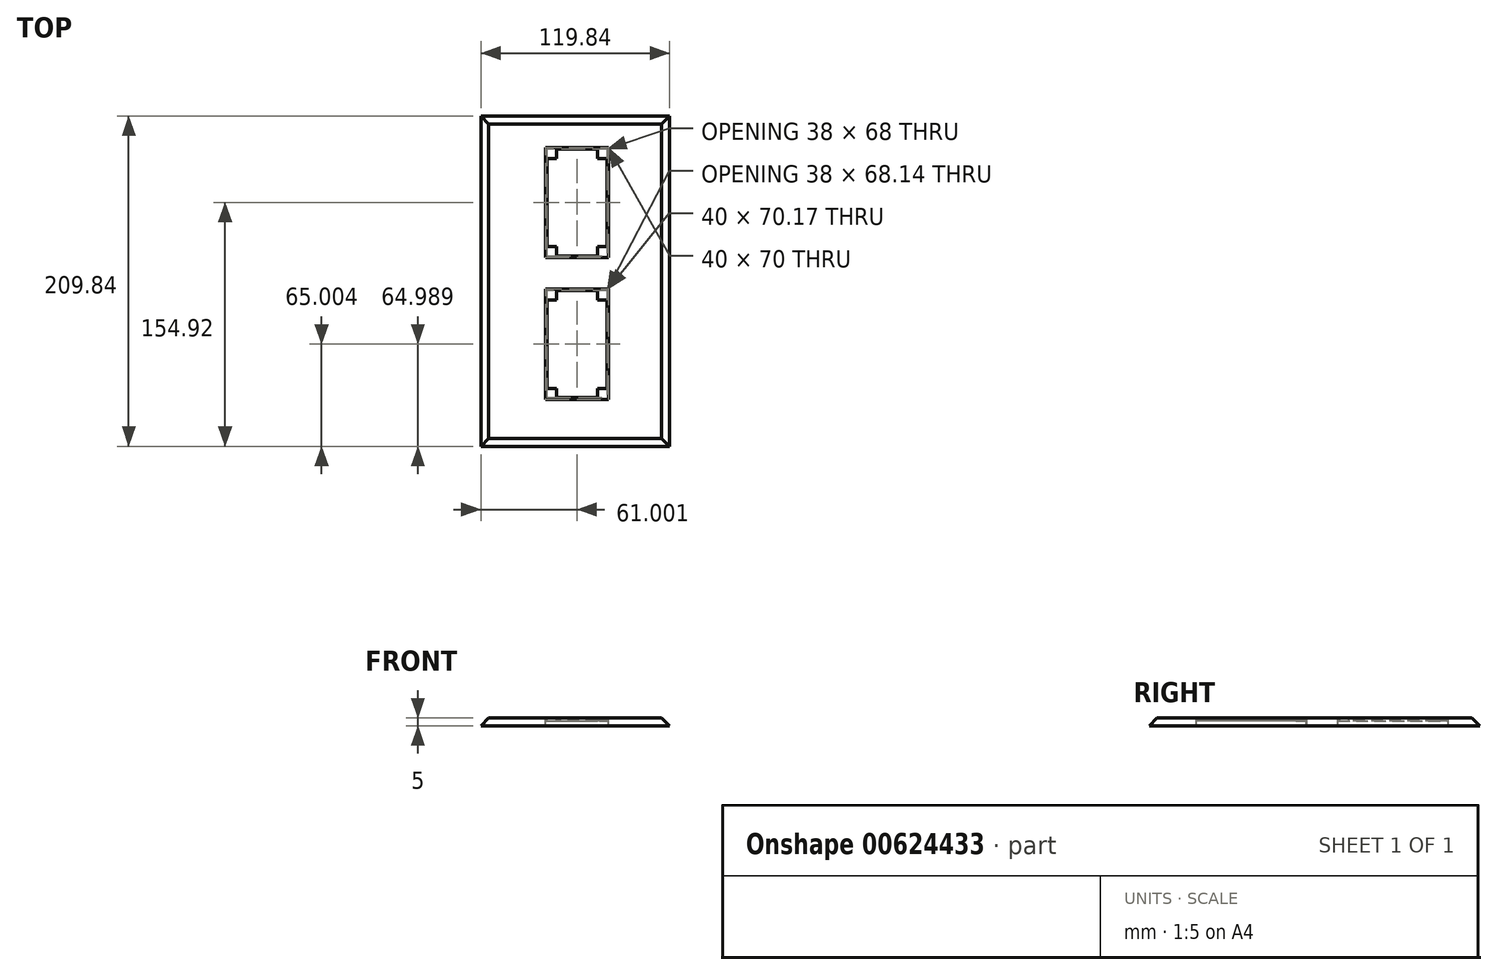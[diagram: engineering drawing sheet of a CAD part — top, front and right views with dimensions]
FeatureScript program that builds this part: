
annotation { "Feature Type Name" : "Feature", "Feature Type Description" : "" }
export const myFeature = defineFeature(function(context is Context, id is Id, definition is map)
    precondition{}
    {
        {
            var Q0;
            Q0=qCreatedBy(makeId("Top.planeOp"),FACE);
            var sketch = newSketch(context, id + "F0", { "sketchPlane" : qUnion([Q0])});
            skLineSegment(sketch, "E0.bottom", {"start": v(60, -105) * mm, "end": v(-60, -105) * mm});
            skLineSegment(sketch, "E0.top", {"start": v(60, 105) * mm, "end": v(-60, 105) * mm});
            skLineSegment(sketch, "E0.left", {"start": v(60, -105) * mm, "end": v(60, 105) * mm});
            skLineSegment(sketch, "E0.right", {"start": v(-60, -105) * mm, "end": v(-60, 105) * mm});
            skPoint(sketch, "E0.middle", {"position": v(0, 0) * mm});
            skLineSegment(sketch, "E1", {"start": v(-18.92, 52.2) * mm, "end": v(-18.92, 85) * mm});
            skLineSegment(sketch, "E2", {"start": v(21.08, 50.97) * mm, "end": v(21.08, 85) * mm});
            skLineSegment(sketch, "E3", {"start": v(21.08, 85) * mm, "end": v(-18.92, 85) * mm});
            skLineSegment(sketch, "E4", {"start": v(-18.92, 85) * mm, "end": v(-18.92, 15) * mm});
            skLineSegment(sketch, "E5", {"start": v(-18.92, 15) * mm, "end": v(21.08, 15) * mm});
            skLineSegment(sketch, "E6", {"start": v(21.08, 15) * mm, "end": v(21.08, 85) * mm});
            skPoint(sketch, "E7.start.orphan", {"position": v(26.42, 105) * mm});
            skPoint(sketch, "E8.orphan", {"position": v(21.08, 105) * mm});
            skLineSegment(sketch, "E9.bottom", {"start": v(-18.92, 85) * mm, "end": v(-11.92, 85) * mm});
            skLineSegment(sketch, "E9.top", {"start": v(-17.92, 78) * mm, "end": v(-11.92, 78) * mm});
            skLineSegment(sketch, "E9.left", {"start": v(-18.92, 85) * mm, "end": v(-18.92, 78) * mm});
            skLineSegment(sketch, "E9.right", {"start": v(-11.92, 84) * mm, "end": v(-11.92, 78) * mm});
            skLineSegment(sketch, "E10.bottom", {"start": v(-18.92, 15) * mm, "end": v(-11.92, 15) * mm});
            skLineSegment(sketch, "E10.top", {"start": v(-17.92, 22) * mm, "end": v(-11.92, 22) * mm});
            skLineSegment(sketch, "E10.left", {"start": v(-18.92, 15) * mm, "end": v(-18.92, 22) * mm});
            skLineSegment(sketch, "E10.right", {"start": v(-11.92, 16) * mm, "end": v(-11.92, 22) * mm});
            skLineSegment(sketch, "E11.bottom", {"start": v(21.08, 85) * mm, "end": v(14.08, 85) * mm});
            skLineSegment(sketch, "E11.top", {"start": v(20.08, 78) * mm, "end": v(14.08, 78) * mm});
            skLineSegment(sketch, "E11.left", {"start": v(21.08, 85) * mm, "end": v(21.08, 78) * mm});
            skLineSegment(sketch, "E11.right", {"start": v(14.08, 84) * mm, "end": v(14.08, 78) * mm});
            skLineSegment(sketch, "E12.bottom", {"start": v(21.08, 15) * mm, "end": v(14.08, 15) * mm});
            skLineSegment(sketch, "E12.top", {"start": v(20.08, 22) * mm, "end": v(14.08, 22) * mm});
            skLineSegment(sketch, "E12.right", {"start": v(14.08, 16) * mm, "end": v(14.08, 22) * mm});
            skLineSegment(sketch, "E13", {"start": v(21.08, -4.83) * mm, "end": v(21.08, -75) * mm});
            skLineSegment(sketch, "E14", {"start": v(1.08, -4.92) * mm, "end": v(1.08, -5) * mm});
            skLineSegment(sketch, "E15", {"start": v(-18.92, -75) * mm, "end": v(21.08, -75) * mm});
            skLineSegment(sketch, "E16", {"start": v(21.08, -4.83) * mm, "end": v(-18.92, -5) * mm});
            skPoint(sketch, "E17.orphan", {"position": v(1.08, 15) * mm});
            skPoint(sketch, "E18.end.orphan", {"position": v(0, -75) * mm});
            skPoint(sketch, "E18.start.orphan", {"position": v(0, -105) * mm});
            skLineSegment(sketch, "E19.0", {"start": v(-11.92, -5.97) * mm, "end": v(-11.92, -11.97) * mm});
            skLineSegment(sketch, "E20", {"start": v(-11.92, -11.97) * mm, "end": v(-17.92, -11.97) * mm});
            skLineSegment(sketch, "E21", {"start": v(14.08, -11.86) * mm, "end": v(20.08, -11.86) * mm});
            skLineSegment(sketch, "E22", {"start": v(14.08, -11.86) * mm, "end": v(14.06, -5.86) * mm});
            skLineSegment(sketch, "E23.0", {"start": v(-17.92, -11.97) * mm, "end": v(-17.92, -68) * mm});
            skLineSegment(sketch, "E24.0", {"start": v(21.08, -5.83) * mm, "end": v(21.08, -5.83) * mm});
            skLineSegment(sketch, "E25.0", {"start": v(20.08, -4.83) * mm, "end": v(20.08, -4.84) * mm});
            skLineSegment(sketch, "E26.trimOffspring", {"start": v(20.08, -11.86) * mm, "end": v(20.08, -68) * mm});
            skLineSegment(sketch, "E27.trimOffspring", {"start": v(14.06, -5.86) * mm, "end": v(-11.92, -5.97) * mm});
            skLineSegment(sketch, "E28.trimOffspring", {"start": v(20.08, 22) * mm, "end": v(20.08, 78) * mm});
            skLineSegment(sketch, "E29.trimOffspring", {"start": v(-11.92, 16) * mm, "end": v(14.08, 16) * mm});
            skLineSegment(sketch, "E30.trimOffspring", {"start": v(-17.92, 78) * mm, "end": v(-17.92, 22) * mm});
            skLineSegment(sketch, "E31.trimOffspring", {"start": v(14.08, 84) * mm, "end": v(-11.92, 84) * mm});
            skLineSegment(sketch, "E32.0", {"start": v(-17.92, -68) * mm, "end": v(-11.92, -68) * mm});
            skLineSegment(sketch, "E33.0", {"start": v(14.08, -4.83) * mm, "end": v(14.08, -11.86) * mm});
            skLineSegment(sketch, "E34.0", {"start": v(-11.92, -5) * mm, "end": v(-11.92, -11.97) * mm});
            skLineSegment(sketch, "E35.trimOffspring", {"start": v(14.08, -68) * mm, "end": v(14.08, -74) * mm});
            skLineSegment(sketch, "E36.trimOffspring", {"start": v(-11.92, -68) * mm, "end": v(-11.92, -74) * mm});
            skLineSegment(sketch, "E37.trimOffspring", {"start": v(14.08, -68) * mm, "end": v(20.08, -68) * mm});
            skLineSegment(sketch, "E38.0", {"start": v(-11.92, -74) * mm, "end": v(14.08, -74) * mm});
            skLineSegment(sketch, "E39", {"start": v(-18.92, -5) * mm, "end": v(-18.92, -75) * mm});
            skSolve(sketch);
        }
        {
            var Q0;
            Q0 = qSketchRegion(id + "F0", true);
            extrude(context, id + "F1", {"entities" : qUnion([Q0]), "oppositeDirection" : true, "depth" : 5 * mm, "offsetDistance" : 25.4 * mm});
        }
        {
            var Q0;
            {var subQ9=sQuery(id+"F0.wireOp",EDGE,"E15");Q0=makeQuery(id+"F0.imprint","IMPRINT",FACE,{"disambiguationData":[TD([[makeQuery(id+"F0.imprint","IMPRINT",EDGE,{"derivedFrom":subQ9}),1.0]])]});}
            var Q1;
            Q1=makeQuery(id+"F0.imprint","IMPRINT",FACE,{"disambiguationData":[TD([[makeQuery(id+"F0.imprint","IMPRINT",EDGE,{"derivedFrom":sQuery(id+"F0.wireOp",EDGE,"E3")}),1.0]])]});
            extrude(context, id + "F2", {"entities" : qUnion([Q0, Q1]), "oppositeDirection" : true, "depth" : 2 * mm, "offsetDistance" : 25.4 * mm});
        }
        {
            var Q0;
            Q0=makeQuery(id+"F1.opExtrude","CAP_EDGE",EDGE,{"disambiguationData":[OSD([sQuery(id+"F0.wireOp",EDGE,"E0.right")])],"isStart":true});
            var Q1;
            Q1=makeQuery(id+"F1.opExtrude","CAP_EDGE",EDGE,{"disambiguationData":[OSD([sQuery(id+"F0.wireOp",EDGE,"E0.left")])],"isStart":true});
            var Q2;
            Q2=makeQuery(id+"F1.opExtrude","CAP_EDGE",EDGE,{"disambiguationData":[OSD([sQuery(id+"F0.wireOp",EDGE,"E0.top")])],"isStart":true});
            var Q3;
            Q3=makeQuery(id+"F1.opExtrude","CAP_EDGE",EDGE,{"disambiguationData":[OSD([sQuery(id+"F0.wireOp",EDGE,"E0.bottom")])],"isStart":true});
            chamfer(context, id + "F3", {"entities" : qUnion([Q0, Q1, Q2, Q3]), "width" : 5.08 * mm, "tangentPropagation" : true});
        }
    });
